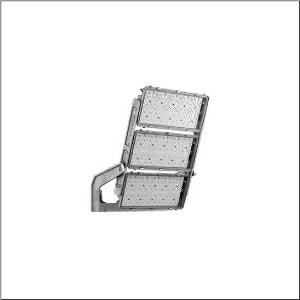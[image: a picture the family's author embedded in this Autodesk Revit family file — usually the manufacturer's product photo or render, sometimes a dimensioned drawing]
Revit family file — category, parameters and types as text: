
# Revit family: floodlight_fl_11_maxi_pro_remote___pl33t_5xa779425t01aa_7d4a
name_source: partatom
category: Lighting Fixtures
units: mm (PartAtom-declared; Revit-internal decimal feet)

## family parameters
Cut with Voids When Loaded = No
Host = Face
Light Source = No
Part Type = Normal
Room Calculation Point = No
Round Connector Dimension = Use Diameter
Shared = No

## types (1)
- --- (1 x LED, 201910 lm, 1539.3 W, 3000K)
    Apparent Load = 1539 VA
    CIE Flux Codes = 27 70 98 100 100
    Color Rendering = 70
    Color Temperature = 3000K
    Default Elevation = 1800 mm
    Description = Floodlight FL 11  maxi  pro Remote floodlight; light control with lens of PMMA; cover panel of toughened safety glass, transparent; light distribution: PL33T, asymmetric direct distribution, LEDcolour temperature: 3000K, rated luminous flux: 201.910lm, colour rendering: CRI > 70, light colour: 730; luminous efficacy: 131lm/W; brightness control: DALI 2 (1 DALI address); with terminal, 8-pole, max. 2.5mm², mains connection: 220..240V/380..400V AC, 50/60Hz, surge voltage resistance: line to ground: 10kV, ECG replaceable separately, no afterglow with DALI off / DMX off command, LED unit replaceable without ESD environment, dustproof LED module, dimming range 10..100%; 1539W floodlight with 2x LED unit of diecast aluminium, coated grey; length: 713mm / width: 651mm / height: 338mm; mounting bracket, of diecast aluminium, uncoated, natural, equipment: Power, protection rating (complete): IP66; insulation class (complete): insulation class I (protective earthing); certification: CE, ENEC, VDE; ball protection: ball impact resistance with accessories, impact resistance: IK07; only for outdoor installations, rated ambient temperature 10°C, permissible operating ambient temperature: -40..+30°C, permissible storage temperature: -40..+85°Cpackaging unit: 1 piece

Light Distribution: PL33T
    Height = 320 mm
    Lamp = 1 x LED
    Lamp Light Flux = 201910 lm
    Lamp Power = 1539.3 W
    Lamp count = 1
    Length = 1002 mm
    Luminous efficacy = 131 lm/W
    Manufacturer = Siteco
    ModVariant = No
    Model = 5XA779425T01AA
    Mounting Place = Ceiling
    Mounting Type = Surface mounted
    Number of Poles = 1
    OnlyDefault = Yes
    Power Factor = 1
    Product Name = Floodlight FL 11 maxi pro Remote | PL33T
    Product group = floodlight | ceiling mounted
    ProductGroupID = 301
    Protection Class = Protection class I
    Protection Degree = IP 66
    RLX_Detail_Level = 1
    RLX_Emergency_Light_Flux = 0 lm
    RLX_Emergency_Type = 0
    RLX_Emergency_Type_DB = No
    RlxData = <blob elided: 52449 chars, md5=8b52c232>
    Socket = socket
    Standby Power = 0 W
    System Light Flux = 201910 lm
    System Power = 1539 W
    Type Comments = factory setting: luminous flux: 100 % | dim-lin: 254 | 1080 mA
    Type Image = l_1349141.jpg
    URL = http://relux.com
    VarID = @adj_079524
    Voltage = 0 V
    Weight = 0.00 kg
    Width = 655 mm

## geometry (parser evidence)
native form markers: Blend x4, Sweep x13
no freeform markers — native parametric forms only
